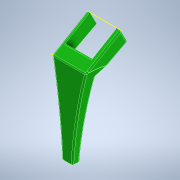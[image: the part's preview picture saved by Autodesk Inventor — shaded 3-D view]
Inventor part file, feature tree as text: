
AUTODESK INVENTOR PART (.ipt)
format: ipt  version: 2022 (Build 260153000, 153)  size: 237,056 bytes
history: native  units: in
note: dims shown in document units (in); Inventor stores cm internally (conversion verified against a paired STEP export)
features: sketch x5, extrude x2, revolve x1, fillet x1
ambient origin geometry x8: Origin, YZ Plane, XZ Plane, XY Plane, X Axis, Y Axis, Z Axis, Center Point
bodies: Solid1 (feature_tree)
feature tree (9):
  extrude  "Extrusion1"  TaperAngle=90.0deg  [1 undecoded]
  revolve  "Revolution1"  [1 undecoded]
  sketch  "Sketch3"
  sketch  "Sketch4"
  sketch  "Sketch5"
  extrude  "Extrusion2"  [1 undecoded]
  fillet  "Fillet1"  [1 undecoded]
  sketch  "Sketch1"  dims[d1=1.9685in d2=0.0in d3=90.0deg]
  sketch  "Sketch2"  dims[d4=1.9685in d5=0.0in d6=0.0787in]
note: 4 required parameter values undecoded (feature->parameter linkage not recoverable at this tier; creation-order binding heuristic only, values carry confidence <= 0.55)